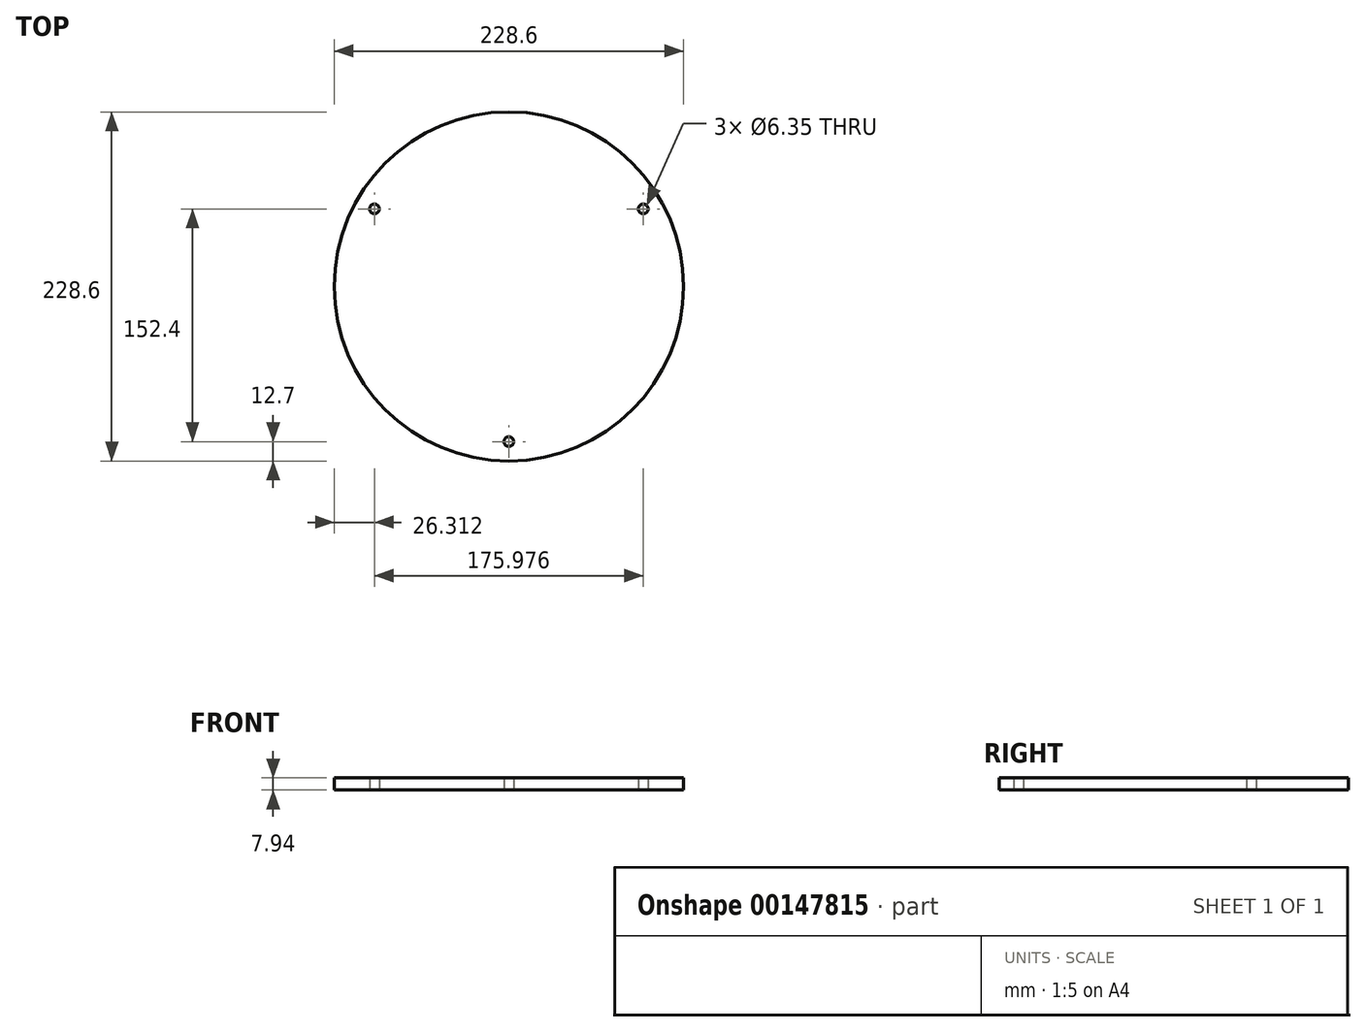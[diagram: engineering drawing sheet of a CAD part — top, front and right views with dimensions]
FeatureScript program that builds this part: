
annotation { "Feature Type Name" : "Feature", "Feature Type Description" : "" }
export const myFeature = defineFeature(function(context is Context, id is Id, definition is map)
    precondition{}
    {
        {
            var Q0;
            Q0=qCreatedBy(makeId("Top.planeOp"),FACE);
            var sketch = newSketch(context, id + "F0", { "sketchPlane" : qUnion([Q0])});
            skCircle(sketch, "E0", {"center": v(0, 0) * mm, "radius": 114.3 * mm});
            skCircle(sketch, "E1.cCircle", {"center": v(0, 0) * mm, "radius": 50.8 * mm, "construction": true});
            skLineSegment(sketch, "E1.0", {"start": v(-87.99, 50.8) * mm, "end": v(87.99, 50.8) * mm, "construction": true});
            skLineSegment(sketch, "E1.1", {"start": v(87.99, 50.8) * mm, "end": v(0, -101.6) * mm, "construction": true});
            skLineSegment(sketch, "E1.2", {"start": v(0, -101.6) * mm, "end": v(-87.99, 50.8) * mm, "construction": true});
            skPoint(sketch, "E1.0.midPoint", {"position": v(0, 50.8) * mm});
            skCircle(sketch, "E2", {"center": v(-87.99, 50.8) * mm, "radius": 12.7 * mm, "construction": true});
            skCircle(sketch, "E3", {"center": v(-87.99, 50.8) * mm, "radius": 3.17 * mm});
            skCircle(sketch, "E4", {"center": v(87.99, 50.8) * mm, "radius": 3.17 * mm});
            skCircle(sketch, "E5", {"center": v(0, -101.6) * mm, "radius": 3.17 * mm});
            skSolve(sketch);
        }
        {
            var Q0;
            Q0=qSketchRegion(id+"F0",true);
            extrude(context, id + "F1", {"entities" : qUnion([Q0]), "depth" : 7.94 * mm});
        }
    });
